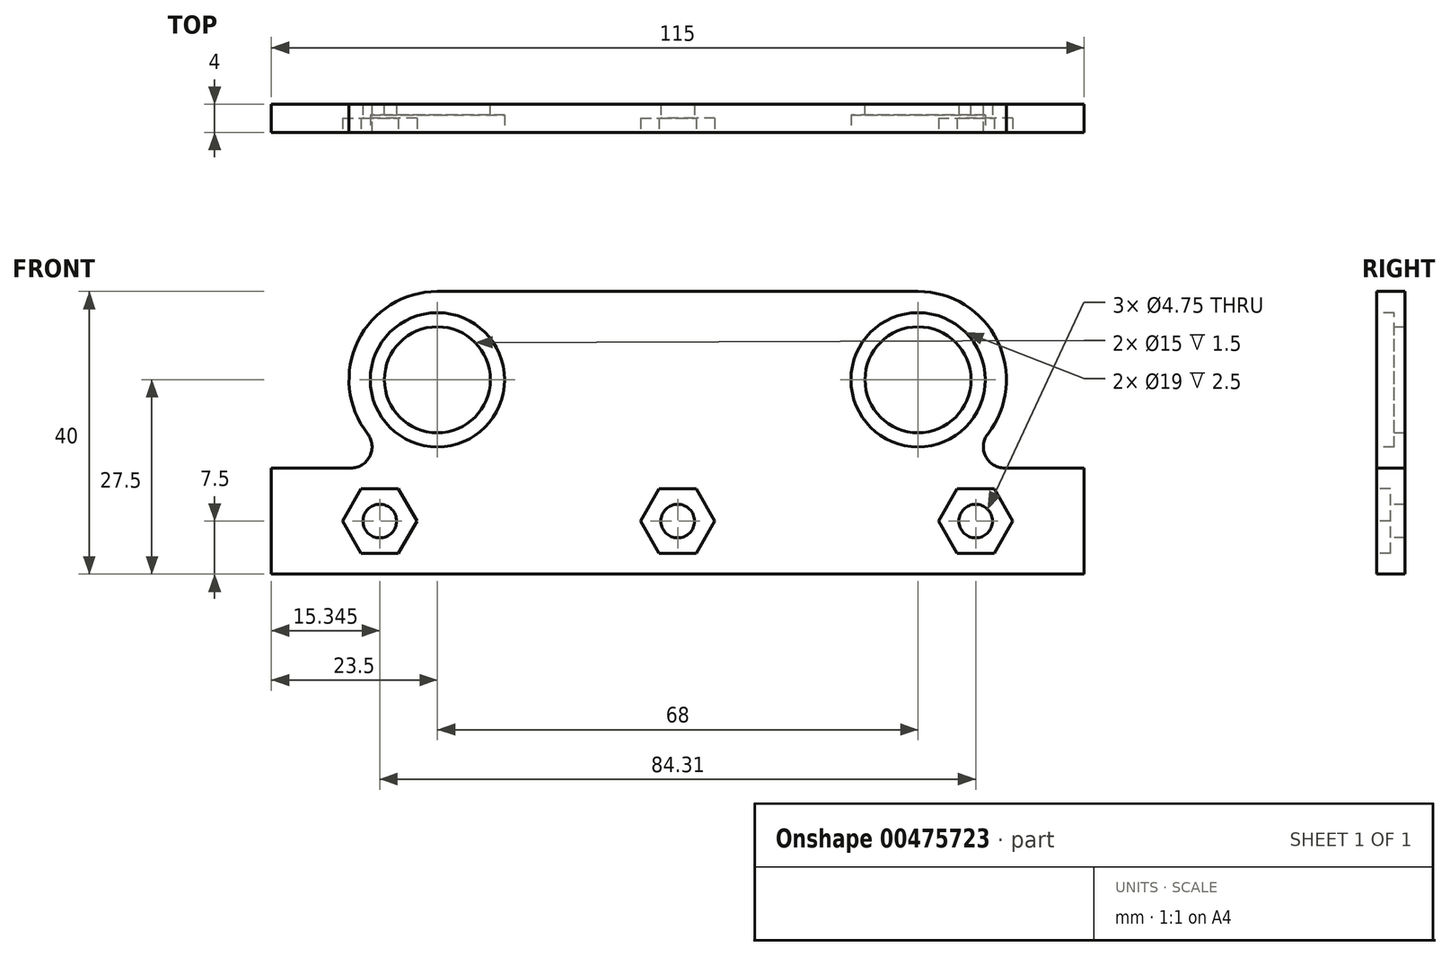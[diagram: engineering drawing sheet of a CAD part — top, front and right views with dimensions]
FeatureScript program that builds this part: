
annotation { "Feature Type Name" : "Feature", "Feature Type Description" : "" }
export const myFeature = defineFeature(function(context is Context, id is Id, definition is map)
    precondition{}
    {
        {
            var Q0;
            Q0=qCreatedBy(makeId("Front.planeOp"),FACE);
            var sketch = newSketch(context, id + "F0", { "sketchPlane" : qUnion([Q0])});
            skCircle(sketch, "E0", {"center": v(-34, 0) * mm, "radius": 7.5 * mm});
            skCircle(sketch, "E1", {"center": v(34, 0) * mm, "radius": 7.5 * mm});
            skCircle(sketch, "E2", {"center": v(-34, 0) * mm, "radius": 12.5 * mm});
            skCircle(sketch, "E3", {"center": v(34, 0) * mm, "radius": 12.5 * mm});
            skLineSegment(sketch, "E4", {"start": v(-34, 12.5) * mm, "end": v(34, 12.5) * mm});
            skLineSegment(sketch, "E5", {"start": v(34, -12.5) * mm, "end": v(-34, -12.5) * mm});
            skLineSegment(sketch, "E6.bottom", {"start": v(57.5, -12.5) * mm, "end": v(-57.5, -12.5) * mm});
            skLineSegment(sketch, "E6.top", {"start": v(57.5, -27.5) * mm, "end": v(-57.5, -27.5) * mm});
            skLineSegment(sketch, "E6.left", {"start": v(57.5, -12.5) * mm, "end": v(57.5, -27.5) * mm});
            skLineSegment(sketch, "E6.right", {"start": v(-57.5, -12.5) * mm, "end": v(-57.5, -27.5) * mm});
            skPoint(sketch, "E6.middle", {"position": v(0, -20) * mm});
            skArc(sketch, "E7", {"start": v(-46.25, -12.5) * mm, "mid": v(-43.55, -10.82) * mm, "end": v(-43.88, -7.66) * mm});
            skArc(sketch, "E8", {"start": v(43.88, -7.66) * mm, "mid": v(43.55, -10.82) * mm, "end": v(46.25, -12.5) * mm});
            skSolve(sketch);
        }
        {
            var Q0;
            Q0=qSketchRegion(id+"F0",true);
            extrude(context, id + "F1", {"entities" : qUnion([Q0]), "depth" : 4 * mm});
        }
        {
            var Q0;
            Q0=makeQuery(id+"F1.opExtrude","CAP_FACE",FACE,{"disambiguationData":[OSD([sQuery(id+"F0.wireOp",EDGE,"E0"),sQuery(id+"F0.wireOp",EDGE,"E1"),sQuery(id+"F0.wireOp",EDGE,"E2"),sQuery(id+"F0.wireOp",EDGE,"E3"),sQuery(id+"F0.wireOp",EDGE,"E4"),sQuery(id+"F0.wireOp",EDGE,"E6.bottom"),sQuery(id+"F0.wireOp",EDGE,"E6.top"),sQuery(id+"F0.wireOp",EDGE,"E6.left"),sQuery(id+"F0.wireOp",EDGE,"E6.right"),sQuery(id+"F0.wireOp",EDGE,"E7"),sQuery(id+"F0.wireOp",EDGE,"E8")])],"isStart":false});
            var sketch = newSketch(context, id + "F2", { "sketchPlane" : qUnion([Q0])});
            skCircle(sketch, "E9", {"center": v(-34, 0) * mm, "radius": 9.5 * mm});
            skCircle(sketch, "E10", {"center": v(34, 0) * mm, "radius": 9.5 * mm});
            skSolve(sketch);
        }
        {
            var Q0;
            Q0=qSketchRegion(id+"F2",true);
            extrude(context, id + "F3", {"entities" : qUnion([Q0]), "operationType" : NewBodyOperationType.REMOVE, "oppositeDirection" : true, "depth" : 2.5 * mm});
        }
        {
            var Q0;
            Q0=makeQuery(id+"F1.opExtrude","CAP_FACE",FACE,{"disambiguationData":[OSD([sQuery(id+"F0.wireOp",EDGE,"E0"),sQuery(id+"F0.wireOp",EDGE,"E1"),sQuery(id+"F0.wireOp",EDGE,"E2"),sQuery(id+"F0.wireOp",EDGE,"E3"),sQuery(id+"F0.wireOp",EDGE,"E4"),sQuery(id+"F0.wireOp",EDGE,"E6.bottom"),sQuery(id+"F0.wireOp",EDGE,"E6.top"),sQuery(id+"F0.wireOp",EDGE,"E6.left"),sQuery(id+"F0.wireOp",EDGE,"E6.right"),sQuery(id+"F0.wireOp",EDGE,"E7"),sQuery(id+"F0.wireOp",EDGE,"E8")])],"isStart":false});
            var sketch = newSketch(context, id + "F4", { "sketchPlane" : qUnion([Q0])});
            skCircle(sketch, "E11", {"center": v(0, -20) * mm, "radius": 2.38 * mm});
            skPoint(sketch, "E11.centerSnap0", {"position": v(-57.5, -20) * mm});
            skCircle(sketch, "E12", {"center": v(42.16, -20) * mm, "radius": 2.38 * mm});
            skCircle(sketch, "E13", {"center": v(-42.16, -20) * mm, "radius": 2.38 * mm});
            skSolve(sketch);
        }
        {
            var Q0;
            Q0=qSketchRegion(id+"F4",true);
            extrude(context, id + "F5", {"entities" : qUnion([Q0]), "operationType" : NewBodyOperationType.REMOVE, "endBound" : BoundingType.THROUGH_ALL, "oppositeDirection" : true, "depth" : 25 * mm});
        }
        {
            var Q0;
            Q0=makeQuery(id+"F1.opExtrude","CAP_FACE",FACE,{"disambiguationData":[OSD([sQuery(id+"F0.wireOp",EDGE,"E0"),sQuery(id+"F0.wireOp",EDGE,"E1"),sQuery(id+"F0.wireOp",EDGE,"E2"),sQuery(id+"F0.wireOp",EDGE,"E3"),sQuery(id+"F0.wireOp",EDGE,"E4"),sQuery(id+"F0.wireOp",EDGE,"E6.bottom"),sQuery(id+"F0.wireOp",EDGE,"E6.top"),sQuery(id+"F0.wireOp",EDGE,"E6.left"),sQuery(id+"F0.wireOp",EDGE,"E6.right"),sQuery(id+"F0.wireOp",EDGE,"E7"),sQuery(id+"F0.wireOp",EDGE,"E8")])],"isStart":false});
            var sketch = newSketch(context, id + "F6", { "sketchPlane" : qUnion([Q0])});
            skCircle(sketch, "E14.cCircle", {"center": v(0, -20) * mm, "radius": 4.55 * mm, "construction": true});
            skLineSegment(sketch, "E14.0", {"start": v(-2.63, -15.45) * mm, "end": v(2.63, -15.45) * mm});
            skLineSegment(sketch, "E14.1", {"start": v(2.63, -15.45) * mm, "end": v(5.25, -20) * mm});
            skLineSegment(sketch, "E14.2", {"start": v(5.25, -20) * mm, "end": v(2.63, -24.55) * mm});
            skLineSegment(sketch, "E14.3", {"start": v(2.63, -24.55) * mm, "end": v(-2.63, -24.55) * mm});
            skLineSegment(sketch, "E14.4", {"start": v(-2.63, -24.55) * mm, "end": v(-5.25, -20) * mm});
            skLineSegment(sketch, "E14.5", {"start": v(-5.25, -20) * mm, "end": v(-2.63, -15.45) * mm});
            skPoint(sketch, "E14.0.midPoint", {"position": v(0, -15.45) * mm});
            skCircle(sketch, "E15.cCircle", {"center": v(-42.16, -20) * mm, "radius": 4.55 * mm, "construction": true});
            skLineSegment(sketch, "E15.0", {"start": v(-44.78, -15.45) * mm, "end": v(-39.53, -15.45) * mm});
            skLineSegment(sketch, "E15.1", {"start": v(-39.53, -15.45) * mm, "end": v(-36.9, -20) * mm});
            skLineSegment(sketch, "E15.2", {"start": v(-36.9, -20) * mm, "end": v(-39.53, -24.55) * mm});
            skLineSegment(sketch, "E15.3", {"start": v(-39.53, -24.55) * mm, "end": v(-44.78, -24.55) * mm});
            skLineSegment(sketch, "E15.4", {"start": v(-44.78, -24.55) * mm, "end": v(-47.4, -20) * mm});
            skLineSegment(sketch, "E15.5", {"start": v(-47.4, -20) * mm, "end": v(-44.78, -15.45) * mm});
            skPoint(sketch, "E15.0.midPoint", {"position": v(-42.16, -15.45) * mm});
            skCircle(sketch, "E16.cCircle", {"center": v(42.16, -20) * mm, "radius": 4.55 * mm, "construction": true});
            skLineSegment(sketch, "E16.0", {"start": v(39.53, -15.45) * mm, "end": v(44.78, -15.45) * mm});
            skLineSegment(sketch, "E16.1", {"start": v(44.78, -15.45) * mm, "end": v(47.4, -20) * mm});
            skLineSegment(sketch, "E16.2", {"start": v(47.4, -20) * mm, "end": v(44.78, -24.55) * mm});
            skLineSegment(sketch, "E16.3", {"start": v(44.78, -24.55) * mm, "end": v(39.53, -24.55) * mm});
            skLineSegment(sketch, "E16.4", {"start": v(39.53, -24.55) * mm, "end": v(36.9, -20) * mm});
            skLineSegment(sketch, "E16.5", {"start": v(36.9, -20) * mm, "end": v(39.53, -15.45) * mm});
            skPoint(sketch, "E16.0.midPoint", {"position": v(42.16, -15.45) * mm});
            skSolve(sketch);
        }
        {
            var Q0;
            Q0=qSketchRegion(id+"F6",true);
            extrude(context, id + "F7", {"entities" : qUnion([Q0]), "operationType" : NewBodyOperationType.REMOVE, "oppositeDirection" : true, "depth" : 2 * mm});
        }
    });
